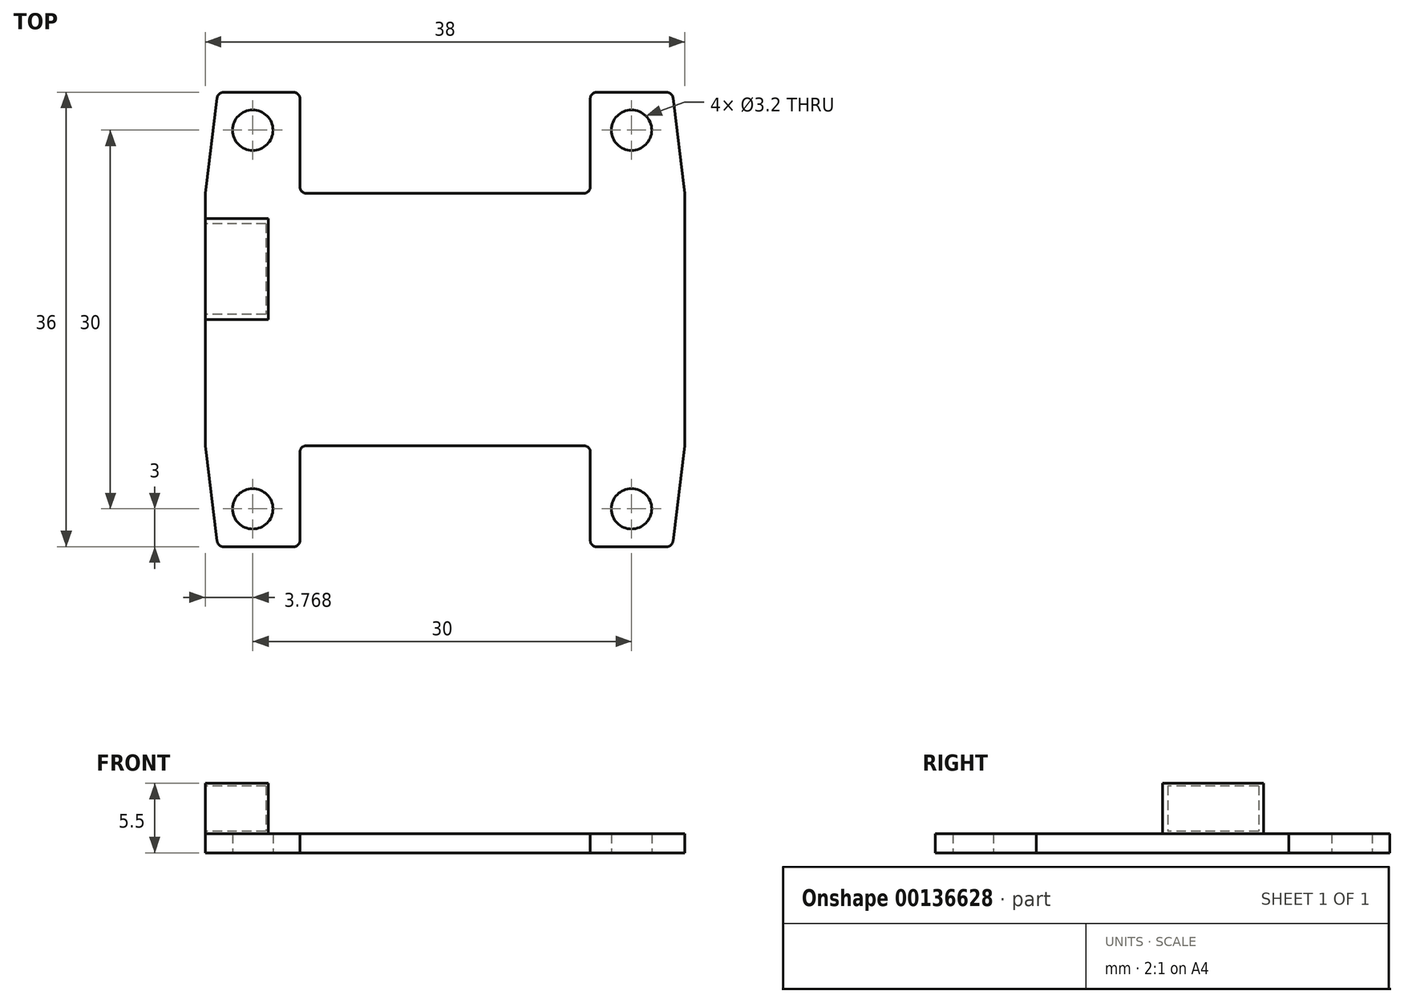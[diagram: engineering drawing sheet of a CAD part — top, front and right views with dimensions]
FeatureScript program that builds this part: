
annotation { "Feature Type Name" : "Feature", "Feature Type Description" : "" }
export const myFeature = defineFeature(function(context is Context, id is Id, definition is map)
    precondition{}
    {
        {
            var Q0;
            Q0=qCreatedBy(makeId("Top.planeOp"),FACE);
            var sketch = newSketch(context, id + "F0", { "sketchPlane" : qUnion([Q0])});
            skPoint(sketch, "E0.middle", {"position": v(0, 0) * mm});
            skPoint(sketch, "E1", {"position": v(-11.5, 18) * mm});
            skPoint(sketch, "E2", {"position": v(11.5, 18) * mm});
            skPoint(sketch, "E3", {"position": v(-11.5, 10) * mm});
            skPoint(sketch, "E4", {"position": v(11.5, 10) * mm});
            skLineSegment(sketch, "E5", {"start": v(-11, 10) * mm, "end": v(11, 10) * mm});
            skLineSegment(sketch, "E6", {"start": v(11.5, 17.5) * mm, "end": v(11.5, 10.5) * mm});
            skLineSegment(sketch, "E7", {"start": v(-11.5, 10.5) * mm, "end": v(-11.5, 17.5) * mm});
            skArc(sketch, "E8.filletArc", {"start": v(-11.5, 10.5) * mm, "mid": v(-11.35, 10.15) * mm, "end": v(-11, 10) * mm});
            skArc(sketch, "E9.filletArc", {"start": v(-11.5, 17.5) * mm, "mid": v(-11.65, 17.85) * mm, "end": v(-12, 18) * mm});
            skArc(sketch, "E10.filletArc", {"start": v(11, 10) * mm, "mid": v(11.35, 10.15) * mm, "end": v(11.5, 10.5) * mm});
            skArc(sketch, "E11.filletArc", {"start": v(12, 18) * mm, "mid": v(11.65, 17.85) * mm, "end": v(11.5, 17.5) * mm});
            skPoint(sketch, "E12", {"position": v(-19, 10) * mm});
            skPoint(sketch, "E13", {"position": v(19, 10) * mm});
            skPoint(sketch, "E14", {"position": v(-18, 18) * mm});
            skPoint(sketch, "E15", {"position": v(18, 18) * mm});
            skLineSegment(sketch, "E16", {"start": v(-18.05, 17.56) * mm, "end": v(-19, 10) * mm});
            skLineSegment(sketch, "E17", {"start": v(18.05, 17.56) * mm, "end": v(19, 10) * mm});
            skLineSegment(sketch, "E18", {"start": v(-17.56, 18) * mm, "end": v(-12, 18) * mm});
            skLineSegment(sketch, "E19", {"start": v(17.56, 18) * mm, "end": v(12, 18) * mm});
            skLineSegment(sketch, "E20", {"start": v(-19, 10) * mm, "end": v(-19, 0) * mm});
            skLineSegment(sketch, "E21", {"start": v(19, 10) * mm, "end": v(19, 0) * mm});
            skArc(sketch, "E22.filletArc", {"start": v(-17.56, 18) * mm, "mid": v(-17.89, 17.87) * mm, "end": v(-18.05, 17.56) * mm});
            skArc(sketch, "E23.filletArc", {"start": v(18.05, 17.56) * mm, "mid": v(17.89, 17.87) * mm, "end": v(17.56, 18) * mm});
            skArc(sketch, "E24.MirrorCS", {"start": v(-11.5, -10.5) * mm, "mid": v(-11.35, -10.15) * mm, "end": v(-11, -10) * mm});
            skArc(sketch, "E25.MirrorCS", {"start": v(18.05, -17.56) * mm, "mid": v(17.89, -17.87) * mm, "end": v(17.56, -18) * mm});
            skArc(sketch, "E26.MirrorCS", {"start": v(-11.5, -17.5) * mm, "mid": v(-11.65, -17.85) * mm, "end": v(-12, -18) * mm});
            skArc(sketch, "E27.MirrorCS", {"start": v(11, -10) * mm, "mid": v(11.35, -10.15) * mm, "end": v(11.5, -10.5) * mm});
            skArc(sketch, "E28.MirrorCS", {"start": v(12, -18) * mm, "mid": v(11.65, -17.85) * mm, "end": v(11.5, -17.5) * mm});
            skArc(sketch, "E29.MirrorCS", {"start": v(-17.56, -18) * mm, "mid": v(-17.89, -17.87) * mm, "end": v(-18.05, -17.56) * mm});
            skPoint(sketch, "E30.MirrorP", {"position": v(11.5, -10) * mm});
            skPoint(sketch, "E31.MirrorP", {"position": v(-11.5, -10) * mm});
            skPoint(sketch, "E32.MirrorP", {"position": v(-18, -18) * mm});
            skPoint(sketch, "E33.MirrorP", {"position": v(11.5, -18) * mm});
            skPoint(sketch, "E34.MirrorP", {"position": v(18, -18) * mm});
            skPoint(sketch, "E35.MirrorP", {"position": v(-11.5, -18) * mm});
            skLineSegment(sketch, "E36.MirrorCS", {"start": v(-19, -10) * mm, "end": v(-19, 0) * mm});
            skLineSegment(sketch, "E37.MirrorCS", {"start": v(-11, -10) * mm, "end": v(11, -10) * mm});
            skLineSegment(sketch, "E38.MirrorCS", {"start": v(11.5, -17.5) * mm, "end": v(11.5, -10.5) * mm});
            skPoint(sketch, "E39.MirrorP", {"position": v(19, -10) * mm});
            skLineSegment(sketch, "E40.MirrorCS", {"start": v(-11.5, -10.5) * mm, "end": v(-11.5, -17.5) * mm});
            skLineSegment(sketch, "E41.MirrorCS", {"start": v(-18.05, -17.56) * mm, "end": v(-19, -10) * mm});
            skLineSegment(sketch, "E42.MirrorCS", {"start": v(17.56, -18) * mm, "end": v(12, -18) * mm});
            skLineSegment(sketch, "E43.MirrorCS", {"start": v(-17.56, -18) * mm, "end": v(-12, -18) * mm});
            skPoint(sketch, "E44.MirrorP", {"position": v(-19, -10) * mm});
            skLineSegment(sketch, "E45.MirrorCS", {"start": v(19, -10) * mm, "end": v(19, 0) * mm});
            skLineSegment(sketch, "E46.MirrorCS", {"start": v(18.05, -17.56) * mm, "end": v(19, -10) * mm});
            skCircle(sketch, "E47", {"center": v(-15.23, 15) * mm, "radius": 1.6 * mm});
            skCircle(sketch, "E48", {"center": v(14.77, 15) * mm, "radius": 1.6 * mm});
            skCircle(sketch, "E49.MirrorC", {"center": v(-15.23, -15) * mm, "radius": 1.6 * mm});
            skCircle(sketch, "E50.MirrorC", {"center": v(14.77, -15) * mm, "radius": 1.6 * mm});
            skSolve(sketch);
        }
        {
            var Q0;
            Q0 = qSketchRegion(id + "F0", true);
            extrude(context, id + "F1", {"entities" : qUnion([Q0]), "endBound" : BoundingType.SYMMETRIC, "depth" : 1.5 * mm});
        }
        {
            var Q0;
            Q0=makeQuery(id+"F1.opExtrude","CAP_FACE",FACE,{"disambiguationData":[OSD([sQuery(id+"F0.wireOp",EDGE,"E5"),sQuery(id+"F0.wireOp",EDGE,"E6"),sQuery(id+"F0.wireOp",EDGE,"E7"),sQuery(id+"F0.wireOp",EDGE,"E8.filletArc"),sQuery(id+"F0.wireOp",EDGE,"E9.filletArc"),sQuery(id+"F0.wireOp",EDGE,"E10.filletArc"),sQuery(id+"F0.wireOp",EDGE,"E11.filletArc"),sQuery(id+"F0.wireOp",EDGE,"E16"),sQuery(id+"F0.wireOp",EDGE,"E17"),sQuery(id+"F0.wireOp",EDGE,"E18"),sQuery(id+"F0.wireOp",EDGE,"E19"),sQuery(id+"F0.wireOp",EDGE,"E20"),sQuery(id+"F0.wireOp",EDGE,"E21"),sQuery(id+"F0.wireOp",EDGE,"E22.filletArc"),sQuery(id+"F0.wireOp",EDGE,"E23.filletArc"),sQuery(id+"F0.wireOp",EDGE,"E24.MirrorCS"),sQuery(id+"F0.wireOp",EDGE,"E25.MirrorCS"),sQuery(id+"F0.wireOp",EDGE,"E26.MirrorCS"),sQuery(id+"F0.wireOp",EDGE,"E27.MirrorCS"),sQuery(id+"F0.wireOp",EDGE,"E28.MirrorCS"),sQuery(id+"F0.wireOp",EDGE,"E29.MirrorCS"),sQuery(id+"F0.wireOp",EDGE,"E36.MirrorCS"),sQuery(id+"F0.wireOp",EDGE,"E37.MirrorCS"),sQuery(id+"F0.wireOp",EDGE,"E38.MirrorCS"),sQuery(id+"F0.wireOp",EDGE,"E40.MirrorCS"),sQuery(id+"F0.wireOp",EDGE,"E41.MirrorCS"),sQuery(id+"F0.wireOp",EDGE,"E42.MirrorCS"),sQuery(id+"F0.wireOp",EDGE,"E43.MirrorCS"),sQuery(id+"F0.wireOp",EDGE,"E45.MirrorCS"),sQuery(id+"F0.wireOp",EDGE,"E46.MirrorCS"),sQuery(id+"F0.wireOp",EDGE,"E47"),sQuery(id+"F0.wireOp",EDGE,"E48"),sQuery(id+"F0.wireOp",EDGE,"E49.MirrorC"),sQuery(id+"F0.wireOp",EDGE,"E50.MirrorC")])],"isStart":false});
            var sketch = newSketch(context, id + "F2", { "sketchPlane" : qUnion([Q0])});
            skLineSegment(sketch, "E51.bottom", {"start": v(-19, 0) * mm, "end": v(-14, 0) * mm});
            skLineSegment(sketch, "E51.top", {"start": v(-19, 8) * mm, "end": v(-14, 8) * mm});
            skLineSegment(sketch, "E51.left", {"start": v(-19, 0) * mm, "end": v(-19, 8) * mm});
            skLineSegment(sketch, "E51.right", {"start": v(-14, 0) * mm, "end": v(-14, 8) * mm});
            skSolve(sketch);
        }
        {
            var Q0;
            Q0 = qSketchRegion(id + "F2", true);
            extrude(context, id + "F3", {"entities" : qUnion([Q0]), "operationType" : NewBodyOperationType.ADD, "depth" : 4 * mm});
        }
        {
            var Q0;
            Q0=makeQuery(id+"F3.boolean.opBoolean","MERGE",FACE,{"derivedFrom":[makeQuery(id+"F1.opExtrude","SWEPT_FACE",FACE,{"disambiguationData":[OSD([sQuery(id+"F0.wireOp",EDGE,"E20"),sQuery(id+"F0.wireOp",EDGE,"E36.MirrorCS")])]}),makeQuery(id+"F3.opExtrude","SWEPT_FACE",FACE,{"disambiguationData":[OSD([sQuery(id+"F2.wireOp",EDGE,"E51.left")])]})]});
            var sketch = newSketch(context, id + "F4", { "sketchPlane" : qUnion([Q0])});
            skLineSegment(sketch, "E52.bottom", {"start": v(-7.6, 4.55) * mm, "end": v(-0.4, 4.55) * mm});
            skLineSegment(sketch, "E52.top", {"start": v(-7.6, 0.95) * mm, "end": v(-0.4, 0.95) * mm});
            skLineSegment(sketch, "E52.left", {"start": v(-7.6, 4.55) * mm, "end": v(-7.6, 0.95) * mm});
            skLineSegment(sketch, "E52.right", {"start": v(-0.4, 4.55) * mm, "end": v(-0.4, 0.95) * mm});
            skSolve(sketch);
        }
        {
            var Q0;
            Q0 = qSketchRegion(id + "F4", true);
            extrude(context, id + "F5", {"entities" : qUnion([Q0]), "operationType" : NewBodyOperationType.REMOVE, "oppositeDirection" : true, "depth" : 4.8 * mm});
        }
    });
